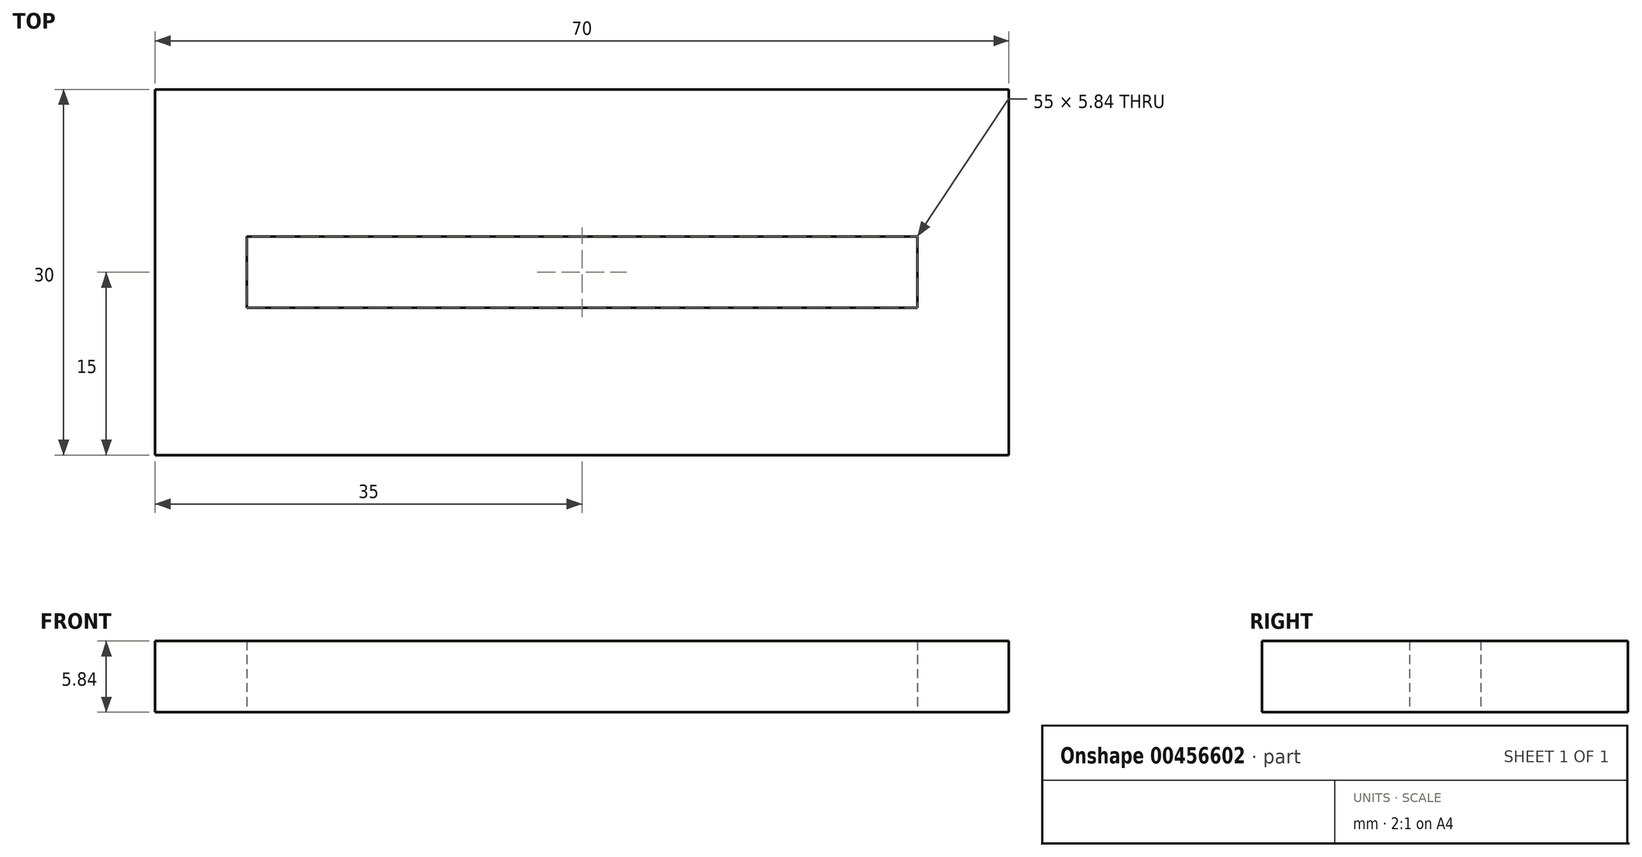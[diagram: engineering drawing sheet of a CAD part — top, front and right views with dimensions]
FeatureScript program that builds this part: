
annotation { "Feature Type Name" : "Feature", "Feature Type Description" : "" }
export const myFeature = defineFeature(function(context is Context, id is Id, definition is map)
    precondition{}
    {
        {
            var Q0;
            Q0=qCreatedBy(makeId("Top.planeOp"),FACE);
            var sketch = newSketch(context, id + "F0", { "sketchPlane" : qUnion([Q0])});
            skLineSegment(sketch, "E0.bottom", {"start": v(35, 15) * mm, "end": v(-35, 15) * mm});
            skLineSegment(sketch, "E0.top", {"start": v(35, -15) * mm, "end": v(-35, -15) * mm});
            skLineSegment(sketch, "E0.left", {"start": v(35, 15) * mm, "end": v(35, -15) * mm});
            skLineSegment(sketch, "E0.right", {"start": v(-35, 15) * mm, "end": v(-35, -15) * mm});
            skPoint(sketch, "E0.middle", {"position": v(0, 0) * mm});
            skLineSegment(sketch, "E1.bottom", {"start": v(27.5, 2.92) * mm, "end": v(-27.5, 2.92) * mm});
            skLineSegment(sketch, "E1.top", {"start": v(27.5, -2.92) * mm, "end": v(-27.5, -2.92) * mm});
            skLineSegment(sketch, "E1.left", {"start": v(27.5, 2.92) * mm, "end": v(27.5, -2.92) * mm});
            skLineSegment(sketch, "E1.right", {"start": v(-27.5, 2.92) * mm, "end": v(-27.5, -2.92) * mm});
            skSolve(sketch);
        }
        {
            var Q0;
            Q0=makeQuery(id+"F0.imprint","IMPRINT",FACE,{"disambiguationData":[TD([[makeQuery(id+"F0.imprint","IMPRINT",EDGE,{"derivedFrom":sQuery(id+"F0.wireOp",EDGE,"E0.bottom")}),1.0]])]});
            extrude(context, id + "F1", {"entities" : qUnion([Q0]), "depth" : 5.84 * mm});
        }
    });
